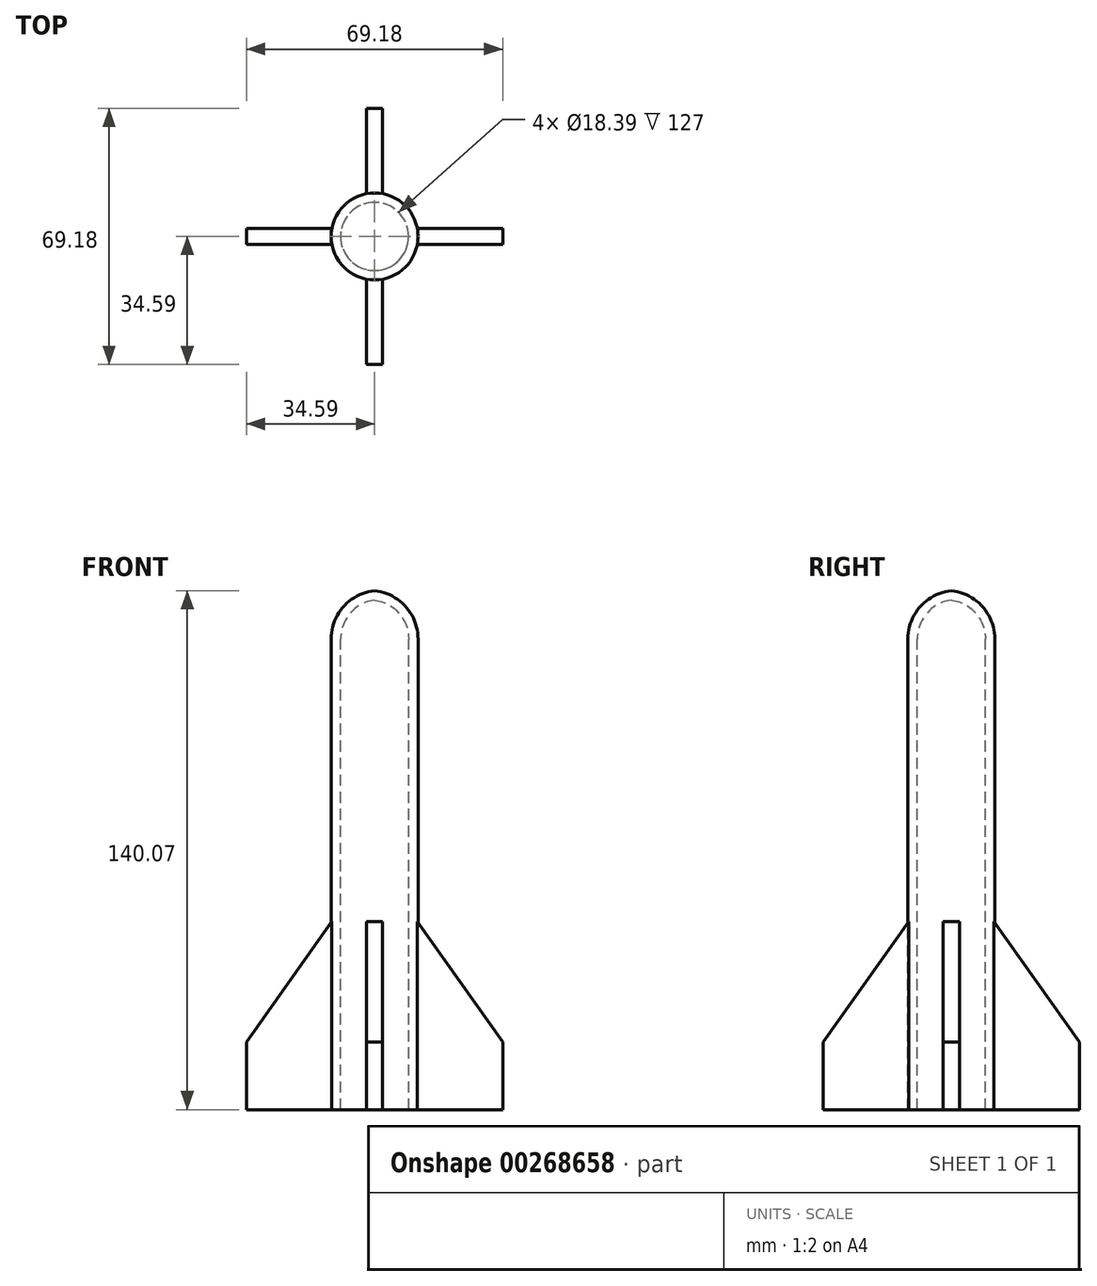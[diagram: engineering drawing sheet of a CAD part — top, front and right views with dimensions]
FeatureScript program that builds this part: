
annotation { "Feature Type Name" : "Feature", "Feature Type Description" : "" }
export const myFeature = defineFeature(function(context is Context, id is Id, definition is map)
    precondition{}
    {
        {
            var Q0;
            Q0=qCreatedBy(makeId("Right.planeOp"),FACE);
            var sketch = newSketch(context, id + "F0", { "sketchPlane" : qUnion([Q0])});
            skLineSegment(sketch, "E0", {"start": v(0, 140.07) * mm, "end": v(0, 137.53) * mm});
            skLineSegment(sketch, "E1", {"start": v(0, 137.53) * mm, "end": v(0, 0) * mm, "construction": true});
            skLineSegment(sketch, "E2", {"start": v(0, 0) * mm, "end": v(-11.73, 0) * mm, "construction": true});
            skLineSegment(sketch, "E3", {"start": v(-11.73, 0) * mm, "end": v(-11.73, 127) * mm});
            skArc(sketch, "E4", {"start": v(0, 140.07) * mm, "mid": v(-8.37, 135.78) * mm, "end": v(-11.73, 127) * mm});
            skLineSegment(sketch, "E5", {"start": v(-11.73, 127) * mm, "end": v(-9.2, 127) * mm});
            skLineSegment(sketch, "E6", {"start": v(-9.2, 127) * mm, "end": v(-9.2, 0) * mm});
            skLineSegment(sketch, "E7", {"start": v(-9.2, 0) * mm, "end": v(-11.73, 0) * mm});
            skArc(sketch, "E8", {"start": v(0, 137.53) * mm, "mid": v(-6.57, 133.99) * mm, "end": v(-9.2, 127) * mm});
            skSolve(sketch);
        }
        {
            var Q0;
            Q0=makeQuery(id+"F0.imprint","IMPRINT",FACE,{"disambiguationData":[TD([[makeQuery(id+"F0.imprint","IMPRINT",EDGE,{"derivedFrom":sQuery(id+"F0.wireOp",EDGE,"E3")}),-1.0]])]});
            var Q1;
            Q1=makeQuery(id+"F0.imprint","IMPRINT",FACE,{"disambiguationData":[TD([[makeQuery(id+"F0.imprint","IMPRINT",EDGE,{"derivedFrom":sQuery(id+"F0.wireOp",EDGE,"E0")}),-1.0]])]});
            var Q2;
            Q2=sQuery(id+"F0.wireOp",EDGE,"E1");
            revolve(context, id + "F1", {"entities" : qUnion([Q0, Q1]), "axis" : qUnion([Q2]), "revolveType" : RevolveType.FULL});
        }
        {
            var Q0;
            Q0=qCreatedBy(makeId("Top.planeOp"),FACE);
            var sketch = newSketch(context, id + "F2", { "sketchPlane" : qUnion([Q0])});
            skLineSegment(sketch, "E9.bottom", {"start": v(2.17, -34.6) * mm, "end": v(-2.17, -34.6) * mm});
            skLineSegment(sketch, "E9.top", {"start": v(2.17, -9.2) * mm, "end": v(-2.17, -9.2) * mm});
            skLineSegment(sketch, "E9.left", {"start": v(2.17, -34.6) * mm, "end": v(2.17, -9.2) * mm});
            skLineSegment(sketch, "E9.right", {"start": v(-2.17, -34.6) * mm, "end": v(-2.17, -9.2) * mm});
            skPoint(sketch, "E9.middle", {"position": v(0, -21.9) * mm});
            skSolve(sketch);
        }
        {
            var Q0;
            Q0 = qSketchRegion(id + "F2", true);
            extrude(context, id + "F3", {"entities" : qUnion([Q0]), "operationType" : NewBodyOperationType.ADD, "depth" : 50.8 * mm});
        }
        {
            var Q0;
            Q0=makeQuery(id+"F3.opExtrude","SWEPT_FACE",FACE,{"disambiguationData":[OSD([sQuery(id+"F2.wireOp",EDGE,"E9.left")])]});
            var sketch = newSketch(context, id + "F4", { "sketchPlane" : qUnion([Q0])});
            skLineSegment(sketch, "E10", {"start": v(-11.53, 50.8) * mm, "end": v(-34.6, 18.3) * mm});
            skLineSegment(sketch, "E11", {"start": v(-34.6, 18.3) * mm, "end": v(-34.6, 50.8) * mm});
            skLineSegment(sketch, "E12", {"start": v(-34.6, 50.8) * mm, "end": v(-11.53, 50.8) * mm});
            skSolve(sketch);
        }
        {
            var Q0;
            Q0 = qSketchRegion(id + "F4", true);
            extrude(context, id + "F5", {"entities" : qUnion([Q0]), "operationType" : NewBodyOperationType.REMOVE, "oppositeDirection" : true, "depth" : 25.4 * mm});
        }
        {
            var Q0;
            Q0=makeQuery(id+"F1.opRevolve","SWEPT_BODY",BODY,{"disambiguationData":[OSD([sQuery(id+"F0.wireOp",EDGE,"E0"),sQuery(id+"F0.wireOp",EDGE,"E3"),sQuery(id+"F0.wireOp",EDGE,"E4"),sQuery(id+"F0.wireOp",EDGE,"E6"),sQuery(id+"F0.wireOp",EDGE,"E7"),sQuery(id+"F0.wireOp",EDGE,"E8")])]});
            var Q1;
            Q1=makeQuery(id+"F1.opRevolve","SWEPT_EDGE",EDGE,{"disambiguationData":[OSD([sQuery(id+"F0.wireOp",EDGE,"E6"),sQuery(id+"F0.wireOp",EDGE,"E7")])]});
            circularPattern(context, id + "F6", {"entities" : qUnion([Q0]), "axis" : qUnion([Q1]), "angle" : 360 * degree, "instanceCount" : 4, "equalSpace" : true});
        }
    });
